# Revit family: CONV_Zero_GnrlPrpseLmnrs_PXLWall
name_source: partatom
category: Lighting Fixtures
revit_build: Autodesk Revit 2015 (Build: 20140905_0730(x64)
units: mm (PartAtom-declared; Revit-internal decimal feet)

## types (4) — shared parameters
AssetType = Fixed
BIMObjectName = CONV_Zero_GnrlPrpseLmnrs_PXLWall
Brand = Zero
Category = Wall
Collection = PXL
Color Filter = 16777215
ConvergoRefNr = 0046-1708-0079-SE
Designer = Fredrik Mattson
Dimming = None
Dimming Lamp Color Temperature Shift = <None>
DurationUnit = Year
Emit Shape Visible in Rendering = No
Emit from Rectangle Length = 1219 mm
Emit from Rectangle Width = 610 mm
ExpiringDate = 08/2018
Features = Snap-in terminal block 3x4mm2. Knockout for external mains cable from above
Finish = Painted metal
HasProtectiveEarth = Yes
IP_Code = IP44
IfcExportAs = IfcLightFixtureType
IfcExportType = NOTDEFINED
LightFixtureMountingType = Surface
LightFixturePlacingType = Wall
Manufacturer = Zero
ManufacturerName = Zero
ManufacturerURL = https://www.zerolighting.com
Material = Metal
NBSDescription = General purpose luminaires
NBSReference = 90-60-50/405
Name = GnrlPrpseLmnrs_PXLWall
NominalCurrent = 0 A
NominalFrequencyRange = 50 Hz
NominalHeight = 190 mm
NominalLength = 350 mm  [stored 1.14829 ft]
NominalVoltage = 230 V
NominalVoltageCalc = 0 V
NominalWidth = 230 mm  [stored 0.754593 ft]
NumberOfPoles = 1
PhaseAngle = 0.00°
Photometric Web File = PXL7795-1.IES
Shape = Sculptured
Size = 350x230x190 mm
Tilt Angle = 0.00°
TotalWattage = 8 W
URL = https://www.zerolighting.com
Uniclass2 = Pr_70_70_49
Uniclass2015Description = Surface luminaires
Uniclass2015Reference = Pr_70_70_48_85
UsageCurrent = 0 A
Version = 1
VersionDate = 07/02/2018
WarrantyDurationUnit = Year
Weight = 1.5 kg
zero-valued in all types: Default Elevation, ElectricalDeviceNominalPower, MaintenanceFactor, NumberOfSources

## per-type parameters (varying)
| type | ArticleNumber | Color | LightFixtureMainMaterial | Model | ModelNumber |
| LED 8W White | 7795-1-01 | White | White Metal | PXL wall LED 8W White | 7795-1-01 |
| E27/max 20W Galvanized | 7773-1-83 | Metallic | Galvanized Metal | PXL wall E27/max 20W Galvanized | 7773-1-83 |
| E27/max 20W White | 7773-1-01 | White | White Metal | PXL wall E27/max 20W White | 7773-1-01 |
| LED 8W Galvanized | 7795-1-83 | Metallic | Galvanized Metal | PXL wall LED 8W Galvanized | 7795-1-83 |

note: [stored X ft] marks values corroborated as IEEE doubles in the binary element streams (Revit-internal decimal feet)

## geometry (parser evidence)
native form markers: Sweep x4
no freeform markers — native parametric forms only
